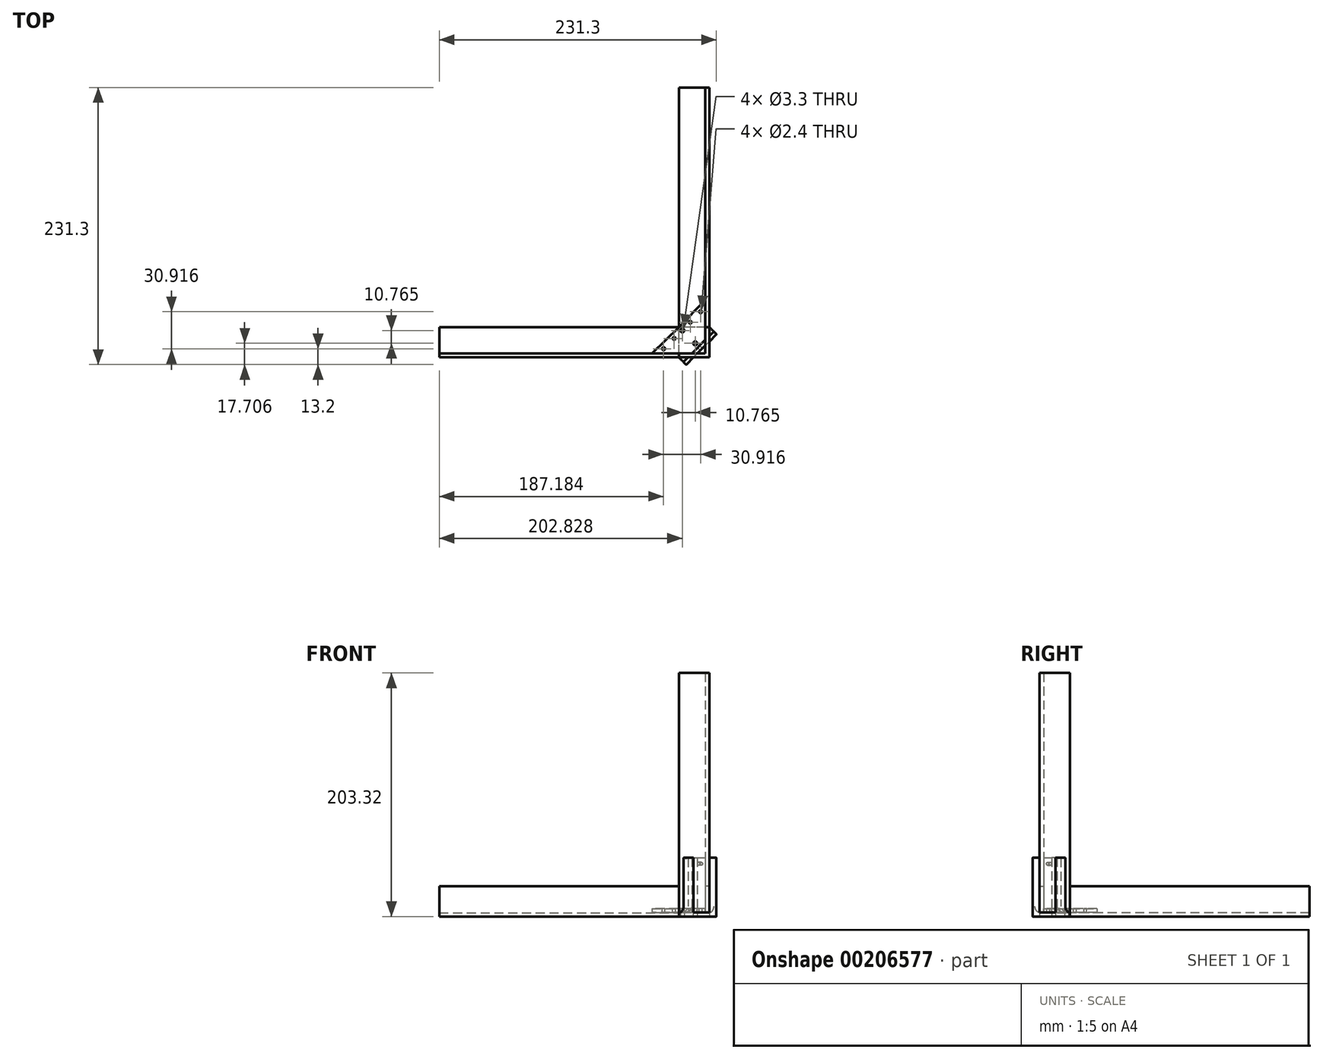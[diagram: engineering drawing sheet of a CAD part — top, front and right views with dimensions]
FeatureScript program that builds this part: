
annotation { "Feature Type Name" : "Feature", "Feature Type Description" : "" }
export const myFeature = defineFeature(function(context is Context, id is Id, definition is map)
    precondition{}
    {
        {
            assignVariable(context, id + "F0", {"name" : "EdgeLWidth", "anyValue" : 25.3 * mm});
        }
        {
            assignVariable(context, id + "F1", {"name" : "HolderLWidth", "anyValue" : 49 * mm});
        }
        {
            assignVariable(context, id + "F2", {"name" : "HolderLThickness", "anyValue" : 3.3 * mm});
        }
        {
            var Q0;
            Q0=qCreatedBy(makeId("Top.planeOp"),FACE);
            var sketch = newSketch(context, id + "F3", { "sketchPlane" : qUnion([Q0])});
            skLineSegment(sketch, "E0", {"start": v(-3.2, 9.89) * mm, "end": v(-6.54, 6.54) * mm});
            skLineSegment(sketch, "E1", {"start": v(-8.88, 8.88) * mm, "end": v(-3.2, 14.56) * mm});
            skLineSegment(sketch, "E2", {"start": v(-3.2, 14.56) * mm, "end": v(-3.2, 9.89) * mm});
            skLineSegment(sketch, "E3", {"start": v(0, 13.09) * mm, "end": v(0, 17.76) * mm});
            skLineSegment(sketch, "E4", {"start": v(0, 17.76) * mm, "end": v(3.77, 21.53) * mm});
            skLineSegment(sketch, "E5", {"start": v(3.77, 21.53) * mm, "end": v(6.1, 19.2) * mm});
            skLineSegment(sketch, "E6", {"start": v(6.1, 19.2) * mm, "end": v(0, 13.09) * mm});
            skLineSegment(sketch, "E7", {"start": v(0, 0) * mm, "end": v(-77.69, 77.69) * mm, "construction": true});
            skLineSegment(sketch, "E8", {"start": v(-77.76, 0) * mm, "end": v(0, 0) * mm, "construction": true});
            skLineSegment(sketch, "E9", {"start": v(0, 0) * mm, "end": v(0, 78.06) * mm, "construction": true});
            skLineSegment(sketch, "E10", {"start": v(6.1, 19.2) * mm, "end": v(-6.54, 6.54) * mm});
            skLineSegment(sketch, "E11.MirrorCS", {"start": v(-19.2, -6.1) * mm, "end": v(-13.09, 0) * mm});
            skLineSegment(sketch, "E12.MirrorCS", {"start": v(-9.89, 3.2) * mm, "end": v(-6.54, 6.54) * mm});
            skLineSegment(sketch, "E13.MirrorCS", {"start": v(-17.76, 0) * mm, "end": v(-21.53, -3.77) * mm});
            skLineSegment(sketch, "E14.MirrorCS", {"start": v(-8.88, 8.88) * mm, "end": v(-14.56, 3.2) * mm});
            skLineSegment(sketch, "E15.MirrorCS", {"start": v(-13.09, 0) * mm, "end": v(-17.76, 0) * mm});
            skLineSegment(sketch, "E16.MirrorCS", {"start": v(-21.53, -3.77) * mm, "end": v(-19.2, -6.1) * mm});
            skLineSegment(sketch, "E17.MirrorCS", {"start": v(-19.2, -6.1) * mm, "end": v(-6.54, 6.54) * mm});
            skLineSegment(sketch, "E18.MirrorCS", {"start": v(-14.56, 3.2) * mm, "end": v(-9.89, 3.2) * mm});
            skPoint(sketch, "E19", {"position": v(-11.7, 11.7) * mm});
            skPoint(sketch, "E20", {"position": v(-22.47, 22.47) * mm});
            skLineSegment(sketch, "E21", {"start": v(3.77, 21.53) * mm, "end": v(0, 25.3) * mm});
            skLineSegment(sketch, "E22", {"start": v(0, 25.3) * mm, "end": v(-25.3, 25.3) * mm});
            skLineSegment(sketch, "E23", {"start": v(-25.3, 25.3) * mm, "end": v(-25.3, 0) * mm});
            skLineSegment(sketch, "E24", {"start": v(-25.3, 0) * mm, "end": v(-21.53, -3.77) * mm});
            skSolve(sketch);
        }
        {
            var Q0;
            Q0=qSketchRegion(id+"F3",true);
            extrude(context, id + "F4", {"entities" : qUnion([Q0]), "depth" : getVariable(context, 'HolderLThickness')});
        }
        {
            var Q0;
            {var subQ0=sQuery(id+"F3.wireOp",EDGE,"E3");Q0=makeQuery(id+"F3.imprint","IMPRINT",FACE,{"disambiguationData":[TD([[makeQuery(id+"F3.imprint","IMPRINT",EDGE,{"derivedFrom":subQ0}),-1.0]])]});}
            var Q1;
            Q1=makeQuery(id+"F3.imprint","IMPRINT",FACE,{"disambiguationData":[TD([[makeQuery(id+"F3.imprint","IMPRINT",EDGE,{"derivedFrom":sQuery(id+"F3.wireOp",EDGE,"E1")}),-1.0]])]});
            var Q2;
            Q2=makeQuery(id+"F3.imprint","IMPRINT",FACE,{"disambiguationData":[TD([[makeQuery(id+"F3.imprint","IMPRINT",EDGE,{"derivedFrom":sQuery(id+"F3.wireOp",EDGE,"E13.MirrorCS")}),1.0]])]});
            extrude(context, id + "F5", {"entities" : qUnion([Q0, Q1, Q2]), "operationType" : NewBodyOperationType.ADD, "depth" : getVariable(context, 'HolderLWidth')});
        }
        {
            var Q0;
            Q0=sQuery(id+"F3.wireOp",VERTEX,"E19");
            var Q1;
            Q1=sQuery(id+"F3.wireOp",VERTEX,"E20");
            var Q2;
            Q2=makeQuery(id+"F4.opExtrude","SWEPT_BODY",BODY,{"disambiguationData":[OSD([sQuery(id+"F3.wireOp",EDGE,"E5"),sQuery(id+"F3.wireOp",EDGE,"o0lL32gh-OSn4-Vle3-xUkx-KtaRwmzb5psM"),sQuery(id+"F3.wireOp",EDGE,"DVCsqTKq-KYus-YFW3-ZN70-3ISmhOG0B1KU"),sQuery(id+"F3.wireOp",EDGE,"E10"),sQuery(id+"F3.wireOp",EDGE,"bed3d973-7b21-4a2b-b050-399250b5e04a2.MirrorCS"),sQuery(id+"F3.wireOp",EDGE,"bed3d973-7b21-4a2b-b050-399250b5e04a6.MirrorCS"),sQuery(id+"F3.wireOp",EDGE,"E16.MirrorCS"),sQuery(id+"F3.wireOp",EDGE,"E17.MirrorCS")])]});
            hole(context, id + "F6", {"style" : HoleStyle.SIMPLE, "endStyle" : HoleEndStyle.THROUGH, "oppositeDirection" : true, "standardTappedOrClearance" : lookupTablePath({ "standard" : "ISO", "fit" : "Normal", "size" : "M3", "type" : "Clearance" }), "standardBlindInLast" : lookupTablePath({ "fit" : "Standard", "standard" : "ISO", "size" : "M3", "type" : "Clearance" }), "holeDiameter" : 3.3 * mm, "startFromSketch" : true, "locations" : qUnion([Q0, Q1]), "scope" : qUnion([Q2]), "isTappedThrough" : true});
        }
        {
            var Q0;
            Q0=makeQuery(id+"F5.opExtrude","SWEPT_FACE",FACE,{"disambiguationData":[OSD([sQuery(id+"F3.wireOp",EDGE,"E1"),sQuery(id+"F3.wireOp",EDGE,"E14.MirrorCS")])]});
            var sketch = newSketch(context, id + "F7", { "sketchPlane" : qUnion([Q0])});
            skLineSegment(sketch, "E25", {"start": v(0, 49) * mm, "end": v(0, 0) * mm, "construction": true});
            skPoint(sketch, "E26", {"position": v(0, 44) * mm});
            skSolve(sketch);
        }
        {
            var Q0;
            Q0=sQuery(id+"F7.wireOp",VERTEX,"E26");
            var Q1;
            Q1=makeQuery(id+"F4.opExtrude","SWEPT_BODY",BODY,{"disambiguationData":[OSD([sQuery(id+"F3.wireOp",EDGE,"E5"),sQuery(id+"F3.wireOp",EDGE,"o0lL32gh-OSn4-Vle3-xUkx-KtaRwmzb5psM"),sQuery(id+"F3.wireOp",EDGE,"DVCsqTKq-KYus-YFW3-ZN70-3ISmhOG0B1KU"),sQuery(id+"F3.wireOp",EDGE,"E10"),sQuery(id+"F3.wireOp",EDGE,"bed3d973-7b21-4a2b-b050-399250b5e04a2.MirrorCS"),sQuery(id+"F3.wireOp",EDGE,"bed3d973-7b21-4a2b-b050-399250b5e04a6.MirrorCS"),sQuery(id+"F3.wireOp",EDGE,"E16.MirrorCS"),sQuery(id+"F3.wireOp",EDGE,"E17.MirrorCS")])]});
            hole(context, id + "F8", {"style" : HoleStyle.SIMPLE, "endStyle" : HoleEndStyle.THROUGH, "standardTappedOrClearance" : lookupTablePath({ "standard" : "ISO", "engagement" : "75%", "pitch" : "0.6 mm", "size" : "M3", "type" : "Tapped" }), "standardBlindInLast" : lookupTablePath({ "standard" : "ISO", "engagement" : "75%", "pitch" : "0.6 mm", "size" : "M3", "type" : "Tapped" }), "holeDiameter" : 2.4 * mm, "startFromSketch" : true, "locations" : qUnion([Q0]), "scope" : qUnion([Q1]), "isTappedThrough" : true, "showTappedDepth" : true});
        }
        {
            var Q0;
            {var subQ0=sQuery(id+"F3.wireOp",EDGE,"E10");var subQ1=sQuery(id+"F3.wireOp",EDGE,"E5");Q0=makeQuery(id+"F5.boolean.opBoolean","MERGE",EDGE,{"derivedFrom":[makeQuery(id+"F4.opExtrude","SWEPT_EDGE",EDGE,{"disambiguationData":[OSD([subQ1,subQ0])]}),makeQuery(id+"F5.opExtrude","SWEPT_EDGE",EDGE,{"disambiguationData":[OSD([subQ1,subQ0])]})]});}
            var Q1;
            Q1=makeQuery(id+"F5.opExtrude","SWEPT_EDGE",EDGE,{"disambiguationData":[OSD([sQuery(id+"F3.wireOp",EDGE,"E4"),sQuery(id+"F3.wireOp",EDGE,"E5"),sQuery(id+"F3.wireOp",EDGE,"o0lL32gh-OSn4-Vle3-xUkx-KtaRwmzb5psM")])]});
            var Q2;
            Q2=makeQuery(id+"F5.opExtrude","CAP_EDGE",EDGE,{"disambiguationData":[OSD([sQuery(id+"F3.wireOp",EDGE,"E5")])],"isStart":false});
            var Q3;
            Q3=makeQuery(id+"F5.opExtrude","CAP_EDGE",EDGE,{"disambiguationData":[OSD([sQuery(id+"F3.wireOp",EDGE,"E10")])],"isStart":false});
            var Q4;
            Q4=makeQuery(id+"F5.opExtrude","CAP_EDGE",EDGE,{"disambiguationData":[OSD([sQuery(id+"F3.wireOp",EDGE,"E4")])],"isStart":false});
            var Q5;
            Q5=makeQuery(id+"F5.opExtrude","CAP_EDGE",EDGE,{"disambiguationData":[OSD([sQuery(id+"F3.wireOp",EDGE,"E17.MirrorCS")])],"isStart":false});
            var Q6;
            Q6=makeQuery(id+"F5.opExtrude","CAP_EDGE",EDGE,{"disambiguationData":[OSD([sQuery(id+"F3.wireOp",EDGE,"E13.MirrorCS")])],"isStart":false});
            var Q7;
            Q7=makeQuery(id+"F5.opExtrude","CAP_EDGE",EDGE,{"disambiguationData":[OSD([sQuery(id+"F3.wireOp",EDGE,"E16.MirrorCS")])],"isStart":false});
            var Q8;
            {var subQ0=sQuery(id+"F3.wireOp",EDGE,"E17.MirrorCS");var subQ1=sQuery(id+"F3.wireOp",EDGE,"E16.MirrorCS");Q8=makeQuery(id+"F5.boolean.opBoolean","MERGE",EDGE,{"derivedFrom":[makeQuery(id+"F4.opExtrude","SWEPT_EDGE",EDGE,{"disambiguationData":[OSD([subQ1,subQ0])]}),makeQuery(id+"F5.opExtrude","SWEPT_EDGE",EDGE,{"disambiguationData":[OSD([subQ1,subQ0])]})]});}
            var Q9;
            Q9=makeQuery(id+"F5.opExtrude","SWEPT_EDGE",EDGE,{"disambiguationData":[OSD([sQuery(id+"F3.wireOp",EDGE,"bed3d973-7b21-4a2b-b050-399250b5e04a2.MirrorCS"),sQuery(id+"F3.wireOp",EDGE,"E13.MirrorCS"),sQuery(id+"F3.wireOp",EDGE,"E16.MirrorCS")])]});
            fillet(context, id + "F9", {"entities" : qUnion([Q0, Q1, Q2, Q3, Q4, Q5, Q6, Q7, Q8, Q9]), "radius" : .25 * mm, "tangentPropagation" : true, "allowEdgeOverflow" : false});
        }
        {
            var Q0;
            Q0=makeQuery(id+"F4.opExtrude","CAP_FACE",FACE,{"disambiguationData":[OSD([sQuery(id+"F3.wireOp",EDGE,"E5"),sQuery(id+"F3.wireOp",EDGE,"o0lL32gh-OSn4-Vle3-xUkx-KtaRwmzb5psM"),sQuery(id+"F3.wireOp",EDGE,"DVCsqTKq-KYus-YFW3-ZN70-3ISmhOG0B1KU"),sQuery(id+"F3.wireOp",EDGE,"E10"),sQuery(id+"F3.wireOp",EDGE,"bed3d973-7b21-4a2b-b050-399250b5e04a2.MirrorCS"),sQuery(id+"F3.wireOp",EDGE,"bed3d973-7b21-4a2b-b050-399250b5e04a6.MirrorCS"),sQuery(id+"F3.wireOp",EDGE,"E16.MirrorCS"),sQuery(id+"F3.wireOp",EDGE,"E17.MirrorCS")])],"isStart":false});
            var sketch = newSketch(context, id + "F10", { "sketchPlane" : qUnion([Q0])});
            skLineSegment(sketch, "E27", {"start": v(0, 0) * mm, "end": v(0, 25.3) * mm});
            skLineSegment(sketch, "E28", {"start": v(-3.2, 25.3) * mm, "end": v(-3.2, 3.2) * mm});
            skLineSegment(sketch, "E29", {"start": v(-3.2, 3.2) * mm, "end": v(-25.3, 3.2) * mm});
            skLineSegment(sketch, "E30", {"start": v(-25.3, 3.2) * mm, "end": v(-25.3, 0) * mm});
            skLineSegment(sketch, "E31", {"start": v(-25.3, 0) * mm, "end": v(0, 0) * mm});
            skLineSegment(sketch, "E32", {"start": v(-3.2, 25.3) * mm, "end": v(0, 25.3) * mm});
            skSolve(sketch);
        }
        {
            var Q0;
            Q0=qSketchRegion(id+"F10",true);
            extrude(context, id + "F11", {"entities" : qUnion([Q0]), "depth" : 200 * mm});
        }
        {
            var Q0;
            Q0=qCreatedBy(makeId("Right.planeOp"),FACE);
            var sketch = newSketch(context, id + "F12", { "sketchPlane" : qUnion([Q0])});
            skLineSegment(sketch, "E33", {"start": v(0, -0.02) * mm, "end": v(0, 25.28) * mm});
            skLineSegment(sketch, "E34", {"start": v(0, 25.28) * mm, "end": v(3.2, 25.28) * mm});
            skLineSegment(sketch, "E35", {"start": v(3.2, 25.28) * mm, "end": v(3.2, 3.18) * mm});
            skLineSegment(sketch, "E36", {"start": v(3.2, 3.18) * mm, "end": v(25.3, 3.18) * mm});
            skLineSegment(sketch, "E37", {"start": v(25.3, 3.18) * mm, "end": v(25.3, -0.02) * mm});
            skLineSegment(sketch, "E38", {"start": v(0, -0.02) * mm, "end": v(25.3, -0.02) * mm});
            skSolve(sketch);
        }
        {
            var Q0;
            Q0=qSketchRegion(id+"F12",true);
            extrude(context, id + "F13", {"entities" : qUnion([Q0]), "oppositeDirection" : true, "depth" : 200 * mm});
        }
        {
            var Q0;
            Q0=makeQuery(id+"F13.opExtrude","SWEPT_BODY",BODY,{"disambiguationData":[OSD([sQuery(id+"F12.wireOp",EDGE,"E33"),sQuery(id+"F12.wireOp",EDGE,"E34"),sQuery(id+"F12.wireOp",EDGE,"E35"),sQuery(id+"F12.wireOp",EDGE,"E36"),sQuery(id+"F12.wireOp",EDGE,"E37"),sQuery(id+"F12.wireOp",EDGE,"E38")])]});
            var Q1;
            Q1=makeQuery(id+"F13.opExtrude","SWEPT_EDGE",EDGE,{"disambiguationData":[OSD([sQuery(id+"F12.wireOp",EDGE,"E36"),sQuery(id+"F12.wireOp",EDGE,"E37")])]});
            transform(context, id + "F14", {"entities" : qUnion([Q0]), "transformType" : TransformType.TRANSLATION_3D, "dx" : -getVariable(context, 'EdgeLWidth'), "dy" : 0 * mm, "dz" : 0 * mm, "makeCopy" : false});
        }
        {
            var Q0;
            Q0=sQuery(id+"F3.wireOp",EDGE,"E7");
            var Q1;
            Q1=makeQuery(id+"F11.opExtrude","SWEPT_EDGE",EDGE,{"disambiguationData":[OSD([sQuery(id+"F10.wireOp",EDGE,"E27"),sQuery(id+"F10.wireOp",EDGE,"E31")])]});
            cPlane(context, id + "F15", {"entities" : qUnion([Q0, Q1]), "cplaneType" : CPlaneType.LINE_ANGLE, "offset" : 25 * mm, "angle" : 180 * degree, "width" : 150 * mm, "height" : 150 * mm});
        }
        {
            var Q0;
            Q0=makeQuery(id+"F13.opExtrude","SWEPT_BODY",BODY,{"disambiguationData":[OSD([sQuery(id+"F12.wireOp",EDGE,"E33"),sQuery(id+"F12.wireOp",EDGE,"E34"),sQuery(id+"F12.wireOp",EDGE,"E35"),sQuery(id+"F12.wireOp",EDGE,"E36"),sQuery(id+"F12.wireOp",EDGE,"E37"),sQuery(id+"F12.wireOp",EDGE,"E38")])]});
            var Q1;
            Q1=qCreatedBy(id+"F15.planeOp",FACE);
            mirror(context, id + "F16", {"entities" : qUnion([Q0]), "mirrorPlane" : qUnion([Q1])});
        }
        {
            var Q0;
            Q0=makeQuery(id+"F4.opExtrude","CAP_FACE",FACE,{"disambiguationData":[OSD([sQuery(id+"F3.wireOp",EDGE,"E5"),sQuery(id+"F3.wireOp",EDGE,"E10"),sQuery(id+"F3.wireOp",EDGE,"E16.MirrorCS"),sQuery(id+"F3.wireOp",EDGE,"E17.MirrorCS"),sQuery(id+"F3.wireOp",EDGE,"E21"),sQuery(id+"F3.wireOp",EDGE,"E22"),sQuery(id+"F3.wireOp",EDGE,"E23"),sQuery(id+"F3.wireOp",EDGE,"E24")])],"isStart":false});
            var sketch = newSketch(context, id + "F17", { "sketchPlane" : qUnion([Q0])});
            skLineSegment(sketch, "E39", {"start": v(-14.56, 3.2) * mm, "end": v(-47.94, 3.2) * mm});
            skLineSegment(sketch, "E40", {"start": v(-47.94, 3.2) * mm, "end": v(-25.3, 25.3) * mm});
            skLineSegment(sketch, "E41", {"start": v(-8.88, 8.88) * mm, "end": v(-14.56, 3.2) * mm});
            skLineSegment(sketch, "E42.MirrorCS", {"start": v(-8.88, 8.88) * mm, "end": v(-3.2, 14.56) * mm});
            skLineSegment(sketch, "E43.MirrorCS", {"start": v(-3.2, 14.56) * mm, "end": v(-3.2, 47.94) * mm});
            skLineSegment(sketch, "E44.MirrorCS", {"start": v(-3.2, 47.94) * mm, "end": v(-25.3, 25.3) * mm});
            skSolve(sketch);
        }
        {
            var Q0;
            Q0=qSketchRegion(id+"F17",true);
            extrude(context, id + "F18", {"entities" : qUnion([Q0]), "depth" : getVariable(context, 'HolderLThickness')});
        }
        {
            var Q0;
            Q0=makeQuery(id+"F18.opExtrude","CAP_FACE",FACE,{"disambiguationData":[OSD([sQuery(id+"F17.wireOp",EDGE,"E39"),sQuery(id+"F17.wireOp",EDGE,"E40"),sQuery(id+"F17.wireOp",EDGE,"E41"),sQuery(id+"F17.wireOp",EDGE,"E42.MirrorCS"),sQuery(id+"F17.wireOp",EDGE,"E43.MirrorCS"),sQuery(id+"F17.wireOp",EDGE,"E44.MirrorCS")])],"isStart":false});
            var sketch = newSketch(context, id + "F19", { "sketchPlane" : qUnion([Q0])});
            skPoint(sketch, "E45", {"position": v(-22.47, 22.47) * mm});
            skPoint(sketch, "E46", {"position": v(-11.7, 11.7) * mm});
            skPoint(sketch, "E47", {"position": v(-29.3, 15.8) * mm});
            skPoint(sketch, "E48", {"position": v(-38.12, 7.2) * mm});
            skPoint(sketch, "E49.MirrorP", {"position": v(-15.8, 29.3) * mm});
            skPoint(sketch, "E50.MirrorP", {"position": v(-7.2, 38.12) * mm});
            skSolve(sketch);
        }
        {
            var Q0;
            Q0=sQuery(id+"F19.wireOp",VERTEX,"E45");
            var Q1;
            Q1=sQuery(id+"F19.wireOp",VERTEX,"E46");
            var Q2;
            Q2=makeQuery(id+"F18.opExtrude","SWEPT_BODY",BODY,{"disambiguationData":[OSD([sQuery(id+"F17.wireOp",EDGE,"E39"),sQuery(id+"F17.wireOp",EDGE,"E40"),sQuery(id+"F17.wireOp",EDGE,"E41"),sQuery(id+"F17.wireOp",EDGE,"E42.MirrorCS"),sQuery(id+"F17.wireOp",EDGE,"E43.MirrorCS"),sQuery(id+"F17.wireOp",EDGE,"E44.MirrorCS")])]});
            hole(context, id + "F20", {"style" : HoleStyle.SIMPLE, "endStyle" : HoleEndStyle.THROUGH, "standardTappedOrClearance" : lookupTablePath({ "standard" : "ISO", "fit" : "Normal", "size" : "M3", "type" : "Clearance" }), "standardBlindInLast" : lookupTablePath({ "fit" : "Standard", "standard" : "ISO", "size" : "M3", "type" : "Clearance" }), "holeDiameter" : 3.3 * mm, "startFromSketch" : true, "locations" : qUnion([Q0, Q1]), "scope" : qUnion([Q2]), "isTappedThrough" : true});
        }
        {
            var Q0;
            Q0=sQuery(id+"F19.wireOp",VERTEX,"E48");
            var Q1;
            Q1=sQuery(id+"F19.wireOp",VERTEX,"E47");
            var Q2;
            Q2=sQuery(id+"F19.wireOp",VERTEX,"E49.MirrorP");
            var Q3;
            Q3=sQuery(id+"F19.wireOp",VERTEX,"E50.MirrorP");
            var Q4;
            Q4=makeQuery(id+"F18.opExtrude","SWEPT_BODY",BODY,{"disambiguationData":[OSD([sQuery(id+"F17.wireOp",EDGE,"E39"),sQuery(id+"F17.wireOp",EDGE,"E40"),sQuery(id+"F17.wireOp",EDGE,"E41"),sQuery(id+"F17.wireOp",EDGE,"E42.MirrorCS"),sQuery(id+"F17.wireOp",EDGE,"E43.MirrorCS"),sQuery(id+"F17.wireOp",EDGE,"E44.MirrorCS")])]});
            hole(context, id + "F21", {"style" : HoleStyle.SIMPLE, "endStyle" : HoleEndStyle.THROUGH, "standardTappedOrClearance" : lookupTablePath({ "standard" : "ISO", "engagement" : "75%", "pitch" : "0.6 mm", "size" : "M3", "type" : "Tapped" }), "standardBlindInLast" : lookupTablePath({ "standard" : "ISO", "engagement" : "75%", "pitch" : "0.6 mm", "size" : "M3", "type" : "Tapped" }), "holeDiameter" : 2.4 * mm, "locations" : qUnion([Q0, Q1, Q2, Q3]), "scope" : qUnion([Q4]), "isTappedThrough" : true, "showTappedDepth" : true});
        }
        {
            var Q0;
            Q0=makeQuery(id+"F18.opExtrude","CAP_EDGE",EDGE,{"disambiguationData":[OSD([sQuery(id+"F17.wireOp",EDGE,"E41"),sQuery(id+"F17.wireOp",EDGE,"E42.MirrorCS")])],"isStart":true});
            var Q1;
            Q1=makeQuery(id+"F5.boolean.opBoolean","INTERSECT",EDGE,{"derivedFrom":[makeQuery(id+"F4.opExtrude","CAP_FACE",FACE,{"disambiguationData":[OSD([sQuery(id+"F3.wireOp",EDGE,"E5"),sQuery(id+"F3.wireOp",EDGE,"E10"),sQuery(id+"F3.wireOp",EDGE,"E16.MirrorCS"),sQuery(id+"F3.wireOp",EDGE,"E17.MirrorCS"),sQuery(id+"F3.wireOp",EDGE,"E21"),sQuery(id+"F3.wireOp",EDGE,"E22"),sQuery(id+"F3.wireOp",EDGE,"E23"),sQuery(id+"F3.wireOp",EDGE,"E24")])],"isStart":false}),makeQuery(id+"F5.opExtrude","SWEPT_FACE",FACE,{"disambiguationData":[OSD([sQuery(id+"F3.wireOp",EDGE,"E1"),sQuery(id+"F3.wireOp",EDGE,"E14.MirrorCS")])]})]});
            var Q2;
            Q2=makeQuery(id+"F5.boolean.opBoolean","INTERSECT",EDGE,{"derivedFrom":[makeQuery(id+"F4.opExtrude","CAP_FACE",FACE,{"disambiguationData":[OSD([sQuery(id+"F3.wireOp",EDGE,"E5"),sQuery(id+"F3.wireOp",EDGE,"E10"),sQuery(id+"F3.wireOp",EDGE,"E16.MirrorCS"),sQuery(id+"F3.wireOp",EDGE,"E17.MirrorCS"),sQuery(id+"F3.wireOp",EDGE,"E21"),sQuery(id+"F3.wireOp",EDGE,"E22"),sQuery(id+"F3.wireOp",EDGE,"E23"),sQuery(id+"F3.wireOp",EDGE,"E24")])],"isStart":false}),makeQuery(id+"F5.opExtrude","SWEPT_FACE",FACE,{"disambiguationData":[OSD([sQuery(id+"F3.wireOp",EDGE,"E13.MirrorCS")])]})]});
            var Q3;
            Q3=makeQuery(id+"F5.boolean.opBoolean","INTERSECT",EDGE,{"derivedFrom":[makeQuery(id+"F4.opExtrude","CAP_FACE",FACE,{"disambiguationData":[OSD([sQuery(id+"F3.wireOp",EDGE,"E5"),sQuery(id+"F3.wireOp",EDGE,"E10"),sQuery(id+"F3.wireOp",EDGE,"E16.MirrorCS"),sQuery(id+"F3.wireOp",EDGE,"E17.MirrorCS"),sQuery(id+"F3.wireOp",EDGE,"E21"),sQuery(id+"F3.wireOp",EDGE,"E22"),sQuery(id+"F3.wireOp",EDGE,"E23"),sQuery(id+"F3.wireOp",EDGE,"E24")])],"isStart":false}),makeQuery(id+"F5.opExtrude","SWEPT_FACE",FACE,{"disambiguationData":[OSD([sQuery(id+"F3.wireOp",EDGE,"E4")])]})]});
            fillet(context, id + "F22", {"entities" : qUnion([Q0, Q1, Q2, Q3]), "radius" : 5 * mm, "tangentPropagation" : true, "allowEdgeOverflow" : false});
        }
    });
